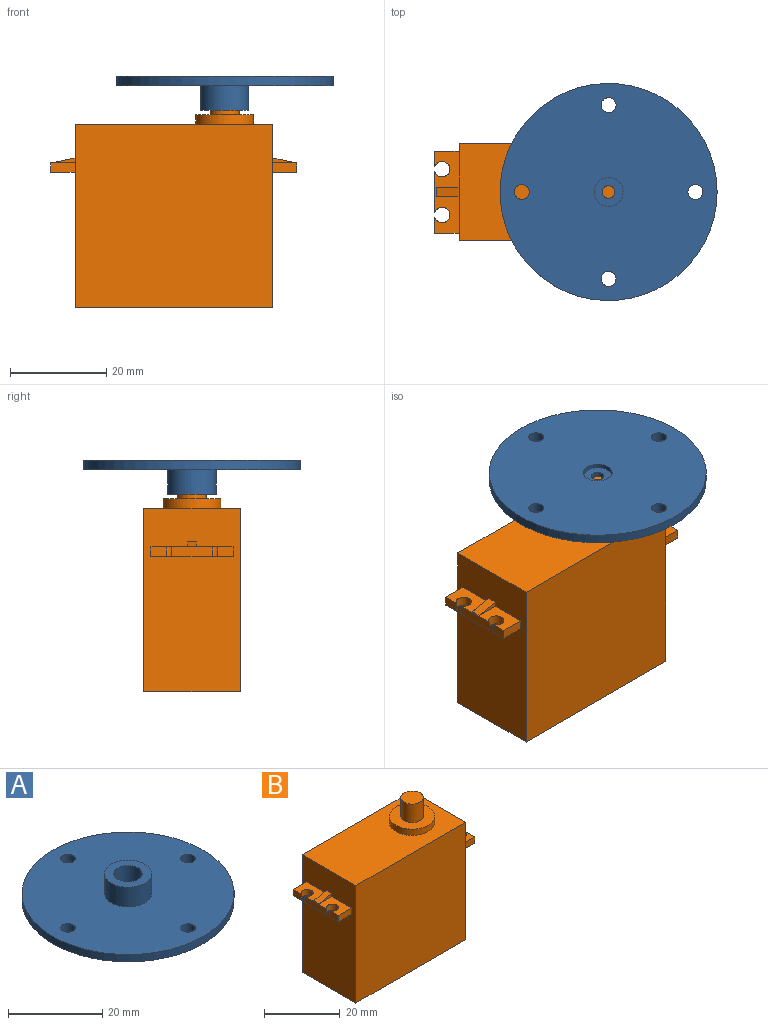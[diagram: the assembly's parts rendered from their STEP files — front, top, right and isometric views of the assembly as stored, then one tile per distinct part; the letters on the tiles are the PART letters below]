
ASSEMBLY  parts=2 mates=1
PART A: 14 faces, bbox 45x45x7 mm
  f0: cylinder r=3mm len=6mm, axis (0,0,-1), area 17mm2, adj f7,f13
  f1: cylinder r=1.55mm len=3.1mm, axis (0,0,-1), area 18.5mm2, adj f6,f7
  f2: cylinder r=1.55mm len=3.1mm, axis (0,0,-1), area 18.5mm2, adj f6,f7
  f3: cylinder r=1.55mm len=3.1mm, axis (0,0,-1), area 18.5mm2, adj f6,f7
  f4: cylinder r=1.55mm len=3.1mm, axis (0,0,-1), area 18.5mm2, adj f6,f7
  f5: cylinder r=22.5mm len=45mm, axis (0,0,-1), area 268.6mm2, adj f6,f7
  f6: plane 45x45mm, normal (0,0,1), area 1481.7mm2, adj f1,f2,f3,f4,f5,f8
  f7: plane 45x45mm, normal (0,0,-1), area 1532mm2, adj f0,f1,f2,f3,f4,f5
  f8: cylinder r=5mm len=10mm, axis (0,0,-1), area 160.2mm2, adj f6,f10
  f9: cylinder r=3mm len=6mm, axis (0,0,-1), area 96.1mm2, adj f10,f12
  f10: plane 10x10mm, normal (0,0,1), area 50.3mm2, adj f8,f9
  f11: cylinder r=1.3mm len=2.6mm, axis (0,0,-1), area 8.2mm2, adj f12,f13
  f12: plane 6x6mm, normal (0,0,1), area 23mm2, adj f9,f11
  f13: plane 6x6mm, normal (0,0,-1), area 23mm2, adj f0,f11
PART B: 34 faces, bbox 51x20x46 mm
  f0: plane 38x20mm, normal (1,0,0), area 724mm2, adj f2,f3,f4,f5,f22,f28,f29,f30
  f1: plane 38x20mm, normal (-1,0,0), area 724mm2, adj f2,f3,f4,f5,f10,f11,f17,f18
  f2: plane 41x38mm, normal (0,-1,0), area 1558mm2, adj f0,f1,f4,f5
  f3: plane 41x38mm, normal (0,1,0), area 1558mm2, adj f0,f1,f4,f5
  f4: plane 41x20mm, normal (0,0,-1), area 820mm2, adj f0,f1,f2,f3
  f5: plane 41x20mm, normal (0,0,1), area 706.9mm2, adj f0,f1,f2,f3,f6
  f6: cylinder r=6mm len=12mm, axis (0,0,-1), area 75.4mm2, adj f5,f7
  f7: plane 12x12mm, normal (0,0,1), area 84.8mm2, adj f6,f8
  f8: cylinder r=3mm len=6mm, axis (0,0,-1), area 113.1mm2, adj f7,f9
  f9: plane 6x6mm, normal (0,0,1), area 28.3mm2, adj f8
  f10: plane 5x2mm, normal (0,-1,0), area 10mm2, adj f1,f16,f17,f18
  f11: plane 5x2mm, normal (0,1,0), area 10mm2, adj f1,f12,f17,f18
  f12: plane 3.19x2mm, normal (-1,0,0), area 6.4mm2, adj f11,f13,f17,f18
  f13: cylinder r=1.6mm len=3.2mm, axis (0,0,1), area 17.8mm2, adj f12,f14,f17,f18
  f14: plane 8.39x2mm, normal (-1,0,0), area 16.8mm2, adj f13,f15,f17,f18
  f15: cylinder r=1.6mm len=3.2mm, axis (0,0,1), area 17.8mm2, adj f14,f16,f17,f18
  f16: plane 3.19x2mm, normal (-1,0,0), area 6.4mm2, adj f10,f15,f17,f18
  f17: plane 17x5mm, normal (0,0,-1), area 69.1mm2, adj f1,f10,f11,f12,f13,f14,f15,f16
  f18: plane 17x5mm, normal (0,0,1), area 59.6mm2, adj f1,f10,f11,f12,f13,f14,f15,f16
  f19: plane 4.75x1mm, normal (0,-1,0), area 2.4mm2, adj f1,f18,f21
  f20: plane 4.75x1mm, normal (0,1,0), area 2.4mm2, adj f1,f18,f21
  f21: plane 4.75x2mm, normal (-0.21,0,0.98), area 9.7mm2, adj f1,f18,f19,f20
  f22: plane 5x2mm, normal (0,-1,0), area 10mm2, adj f0,f23,f29,f30
  f23: plane 3.19x2mm, normal (1,0,0), area 6.4mm2, adj f22,f24,f29,f30
  f24: cylinder r=1.6mm len=3.2mm, axis (0,0,1), area 17.8mm2, adj f23,f25,f29,f30
  f25: plane 8.39x2mm, normal (1,0,0), area 16.8mm2, adj f24,f26,f29,f30
  f26: cylinder r=1.6mm len=3.2mm, axis (0,0,1), area 17.8mm2, adj f25,f27,f29,f30
  f27: plane 3.19x2mm, normal (1,0,0), area 6.4mm2, adj f26,f28,f29,f30
  f28: plane 5x2mm, normal (0,1,0), area 10mm2, adj f0,f27,f29,f30
  f29: plane 17x5mm, normal (0,0,-1), area 69.1mm2, adj f0,f22,f23,f24,f25,f26,f27,f28
  f30: plane 17x5mm, normal (0,0,1), area 59.6mm2, adj f0,f22,f23,f24,f25,f26,f27,f28
  f31: plane 4.75x1mm, normal (0,1,0), area 2.4mm2, adj f0,f30,f33
  f32: plane 4.75x1mm, normal (0,-1,0), area 2.4mm2, adj f0,f30,f33
  f33: plane 4.75x2mm, normal (0.21,0,0.98), area 9.7mm2, adj f0,f30,f31,f32
PLACE A rot(axis=(1,0,0),180deg) t=(10.5,0,9.9)mm
PLACE B at identity fixed
MATE revolute A.f0 <-> B.f6  axis (0,0,1) through (10.5,0,8)mm
